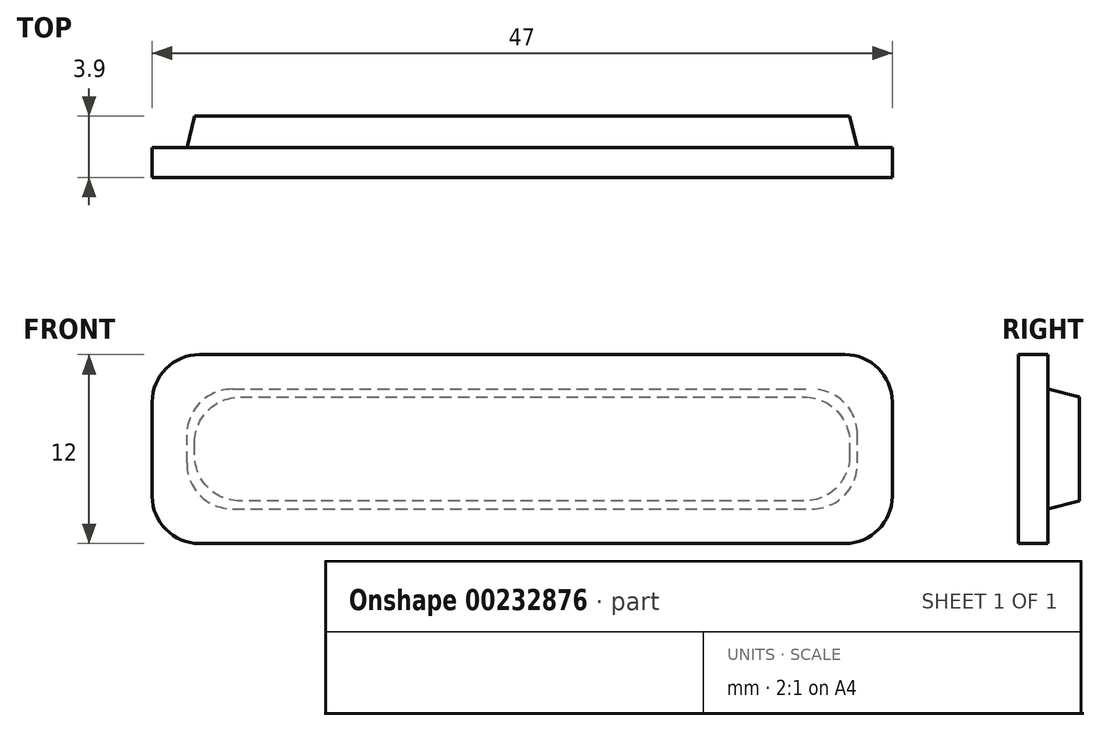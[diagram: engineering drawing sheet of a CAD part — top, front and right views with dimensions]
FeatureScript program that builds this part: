
annotation { "Feature Type Name" : "Feature", "Feature Type Description" : "" }
export const myFeature = defineFeature(function(context is Context, id is Id, definition is map)
    precondition{}
    {
        {
            var Q0;
            Q0=qCreatedBy(makeId("Front.planeOp"),FACE);
            var sketch = newSketch(context, id + "F0", { "sketchPlane" : qUnion([Q0])});
            skLineSegment(sketch, "E0.bottom", {"start": v(23.5, 6) * mm, "end": v(-23.5, 6) * mm});
            skLineSegment(sketch, "E0.top", {"start": v(23.5, -6) * mm, "end": v(-23.5, -6) * mm});
            skLineSegment(sketch, "E0.left", {"start": v(23.5, 6) * mm, "end": v(23.5, -6) * mm});
            skLineSegment(sketch, "E0.right", {"start": v(-23.5, 6) * mm, "end": v(-23.5, -6) * mm});
            skPoint(sketch, "E0.middle", {"position": v(0, 0) * mm});
            skSolve(sketch);
        }
        {
            var Q0;
            Q0 = qSketchRegion(id + "F0", true);
            extrude(context, id + "F1", {"entities" : qUnion([Q0]), "depth" : 1.9 * mm});
        }
        {
            var Q0;
            Q0=makeQuery(id+"F1.opExtrude","CAP_FACE",FACE,{"disambiguationData":[OSD([sQuery(id+"F0.wireOp",EDGE,"E0.bottom"),sQuery(id+"F0.wireOp",EDGE,"E0.top"),sQuery(id+"F0.wireOp",EDGE,"E0.left"),sQuery(id+"F0.wireOp",EDGE,"E0.right")])],"isStart":true});
            var sketch = newSketch(context, id + "F2", { "sketchPlane" : qUnion([Q0])});
            skLineSegment(sketch, "E1.bottom", {"start": v(21.3, -3.8) * mm, "end": v(-21.3, -3.8) * mm});
            skLineSegment(sketch, "E1.top", {"start": v(21.3, 3.8) * mm, "end": v(-21.3, 3.8) * mm});
            skLineSegment(sketch, "E1.left", {"start": v(21.3, -3.8) * mm, "end": v(21.3, 3.8) * mm});
            skLineSegment(sketch, "E1.right", {"start": v(-21.3, -3.8) * mm, "end": v(-21.3, 3.8) * mm});
            skPoint(sketch, "E1.middle", {"position": v(0, 0) * mm});
            skSolve(sketch);
        }
        {
            var Q0;
            Q0=makeQuery(id+"F2.imprint","IMPRINT",FACE,{"disambiguationData":[TD([[makeQuery(id+"F2.imprint","IMPRINT",EDGE,{"derivedFrom":sQuery(id+"F2.wireOp",EDGE,"E1.bottom")}),-1.0]])]});
            extrude(context, id + "F3", {"entities" : qUnion([Q0]), "operationType" : NewBodyOperationType.ADD, "depth" : 2 * mm});
        }
        {
            var Q0;
            Q0=makeQuery(id+"F3.opExtrude","CAP_FACE",FACE,{"disambiguationData":[OSD([sQuery(id+"F2.wireOp",EDGE,"E1.bottom"),sQuery(id+"F2.wireOp",EDGE,"E1.top"),sQuery(id+"F2.wireOp",EDGE,"E1.left"),sQuery(id+"F2.wireOp",EDGE,"E1.right")])],"isStart":false});
            chamfer(context, id + "F4", {"entities" : qUnion([Q0]), "chamferType" : ChamferType.TWO_OFFSETS, "width1" : 0.5 * mm, "oppositeDirection" : true, "width2" : 2 * mm, "tangentPropagation" : true});
        }
        {
            var Q0;
            Q0=makeQuery(id+"F1.opExtrude","SWEPT_EDGE",EDGE,{"disambiguationData":[OSD([sQuery(id+"F0.wireOp",EDGE,"E0.top"),sQuery(id+"F0.wireOp",EDGE,"E0.right")])]});
            var Q1;
            Q1=makeQuery(id+"F1.opExtrude","SWEPT_EDGE",EDGE,{"disambiguationData":[OSD([sQuery(id+"F0.wireOp",EDGE,"E0.top"),sQuery(id+"F0.wireOp",EDGE,"E0.left")])]});
            var Q2;
            Q2=makeQuery(id+"F1.opExtrude","SWEPT_EDGE",EDGE,{"disambiguationData":[OSD([sQuery(id+"F0.wireOp",EDGE,"E0.bottom"),sQuery(id+"F0.wireOp",EDGE,"E0.left")])]});
            var Q3;
            Q3=makeQuery(id+"F1.opExtrude","SWEPT_EDGE",EDGE,{"disambiguationData":[OSD([sQuery(id+"F0.wireOp",EDGE,"E0.bottom"),sQuery(id+"F0.wireOp",EDGE,"E0.right")])]});
            var Q4;
            Q4=makeQuery(id+"F4.opChamfer","BLEND_EDGE",EDGE,{"blendedFrom":[makeQuery(id+"F3.opExtrude","CAP_EDGE",EDGE,{"disambiguationData":[OSD([sQuery(id+"F2.wireOp",EDGE,"E1.top")])],"isStart":false}),makeQuery(id+"F3.opExtrude","CAP_EDGE",EDGE,{"disambiguationData":[OSD([sQuery(id+"F2.wireOp",EDGE,"E1.left")])],"isStart":false})],"blendedInto":[]});
            var Q5;
            Q5=makeQuery(id+"F4.opChamfer","BLEND_EDGE",EDGE,{"blendedFrom":[makeQuery(id+"F3.opExtrude","CAP_EDGE",EDGE,{"disambiguationData":[OSD([sQuery(id+"F2.wireOp",EDGE,"E1.bottom")])],"isStart":false}),makeQuery(id+"F3.opExtrude","CAP_EDGE",EDGE,{"disambiguationData":[OSD([sQuery(id+"F2.wireOp",EDGE,"E1.left")])],"isStart":false})],"blendedInto":[]});
            var Q6;
            Q6=makeQuery(id+"F4.opChamfer","BLEND_EDGE",EDGE,{"blendedFrom":[makeQuery(id+"F3.opExtrude","CAP_EDGE",EDGE,{"disambiguationData":[OSD([sQuery(id+"F2.wireOp",EDGE,"E1.top")])],"isStart":false}),makeQuery(id+"F3.opExtrude","CAP_EDGE",EDGE,{"disambiguationData":[OSD([sQuery(id+"F2.wireOp",EDGE,"E1.right")])],"isStart":false})],"blendedInto":[]});
            var Q7;
            Q7=makeQuery(id+"F4.opChamfer","BLEND_EDGE",EDGE,{"blendedFrom":[makeQuery(id+"F3.opExtrude","CAP_EDGE",EDGE,{"disambiguationData":[OSD([sQuery(id+"F2.wireOp",EDGE,"E1.bottom")])],"isStart":false}),makeQuery(id+"F3.opExtrude","CAP_EDGE",EDGE,{"disambiguationData":[OSD([sQuery(id+"F2.wireOp",EDGE,"E1.right")])],"isStart":false})],"blendedInto":[]});
            fillet(context, id + "F5", {"entities" : qUnion([Q0, Q1, Q2, Q3, Q4, Q5, Q6, Q7]), "radius" : 3 * mm, "tangentPropagation" : true, "allowEdgeOverflow" : false});
        }
    });
